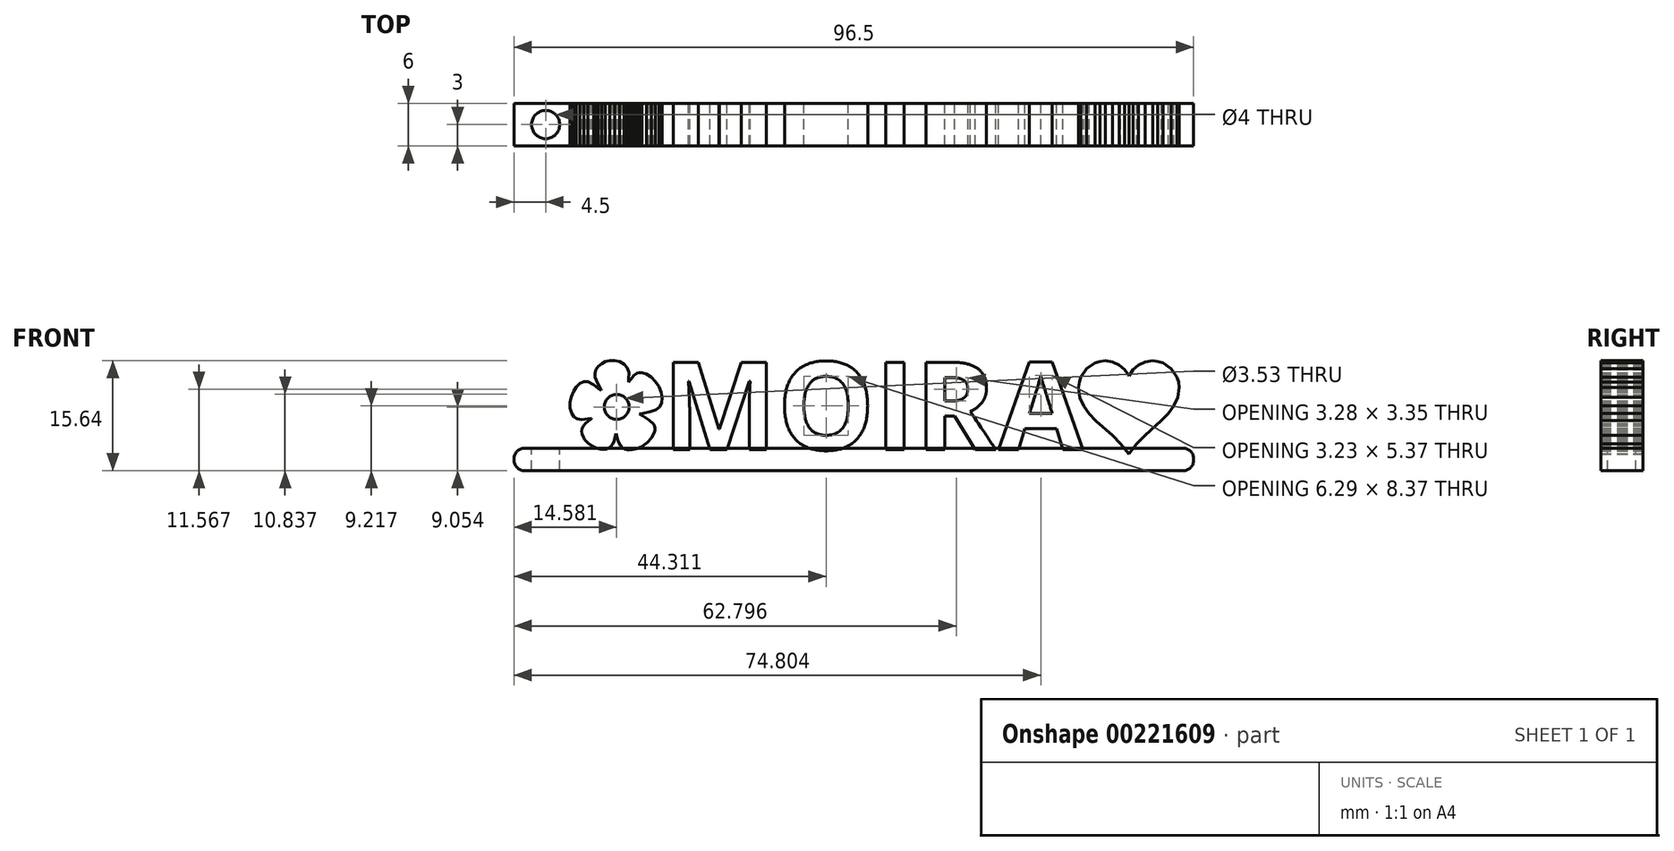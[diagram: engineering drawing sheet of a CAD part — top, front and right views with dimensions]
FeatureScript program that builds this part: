
annotation { "Feature Type Name" : "Feature", "Feature Type Description" : "" }
export const myFeature = defineFeature(function(context is Context, id is Id, definition is map)
    precondition{}
    {
        {
            var Q0;
            Q0=qCreatedBy(makeId("Front.planeOp"),FACE);
            var sketch = newSketch(context, id + "F0", { "sketchPlane" : qUnion([Q0])});
            skText(sketch, "E0", { "text": "   MOIRA", "fontName": "OpenSans-Bold.ttf"});
            skLineSegment(sketch, "E1.0.0", {"start": v(-9.3, 0.1) * mm, "end": v(-8.53, 0.46) * mm});
            skLineSegment(sketch, "E1.0.1", {"start": v(-8.53, 0.46) * mm, "end": v(-7.79, 1.02) * mm});
            skLineSegment(sketch, "E1.0.2", {"start": v(-7.79, 1.02) * mm, "end": v(-7.18, 1.67) * mm});
            skLineSegment(sketch, "E1.0.3", {"start": v(-7.18, 1.67) * mm, "end": v(-6.78, 2.35) * mm});
            skLineSegment(sketch, "E1.0.4", {"start": v(-6.78, 2.35) * mm, "end": v(-6.68, 2.7) * mm});
            skLineSegment(sketch, "E1.0.5", {"start": v(-6.68, 2.7) * mm, "end": v(-6.67, 3.02) * mm});
            skLineSegment(sketch, "E1.0.6", {"start": v(-6.67, 3.02) * mm, "end": v(-6.73, 3.33) * mm});
            skLineSegment(sketch, "E1.0.7", {"start": v(-6.73, 3.33) * mm, "end": v(-6.89, 3.62) * mm});
            skLineSegment(sketch, "E1.0.8", {"start": v(-6.89, 3.62) * mm, "end": v(-7.48, 4.2) * mm});
            skLineSegment(sketch, "E1.0.9", {"start": v(-7.48, 4.2) * mm, "end": v(-8.5, 4.79) * mm});
            skLineSegment(sketch, "E1.0.10", {"start": v(-8.5, 4.79) * mm, "end": v(-8.93, 5.06) * mm});
            skLineSegment(sketch, "E1.0.11", {"start": v(-8.93, 5.06) * mm, "end": v(-8.42, 5.16) * mm});
            skLineSegment(sketch, "E1.0.12", {"start": v(-8.42, 5.16) * mm, "end": v(-7.31, 5.37) * mm});
            skLineSegment(sketch, "E1.0.13", {"start": v(-7.31, 5.37) * mm, "end": v(-6.55, 5.65) * mm});
            skLineSegment(sketch, "E1.0.14", {"start": v(-6.55, 5.65) * mm, "end": v(-6.05, 6.04) * mm});
            skLineSegment(sketch, "E1.0.15", {"start": v(-6.05, 6.04) * mm, "end": v(-5.76, 6.58) * mm});
            skLineSegment(sketch, "E1.0.16", {"start": v(-5.76, 6.58) * mm, "end": v(-5.64, 7.33) * mm});
            skLineSegment(sketch, "E1.0.17", {"start": v(-5.64, 7.33) * mm, "end": v(-5.78, 8.14) * mm});
            skLineSegment(sketch, "E1.0.18", {"start": v(-5.78, 8.14) * mm, "end": v(-6.1, 8.93) * mm});
            skLineSegment(sketch, "E1.0.19", {"start": v(-6.1, 8.93) * mm, "end": v(-6.6, 9.67) * mm});
            skLineSegment(sketch, "E1.0.20", {"start": v(-6.6, 9.67) * mm, "end": v(-7.2, 10.28) * mm});
            skLineSegment(sketch, "E1.0.21", {"start": v(-7.2, 10.28) * mm, "end": v(-7.86, 10.72) * mm});
            skLineSegment(sketch, "E1.0.22", {"start": v(-7.86, 10.72) * mm, "end": v(-8.55, 10.93) * mm});
            skLineSegment(sketch, "E1.0.23", {"start": v(-8.55, 10.93) * mm, "end": v(-8.88, 10.93) * mm});
            skLineSegment(sketch, "E1.0.24", {"start": v(-8.88, 10.93) * mm, "end": v(-9.2, 10.85) * mm});
            skLineSegment(sketch, "E1.0.25", {"start": v(-9.2, 10.85) * mm, "end": v(-9.65, 10.56) * mm});
            skLineSegment(sketch, "E1.0.26", {"start": v(-9.65, 10.56) * mm, "end": v(-10.14, 9.98) * mm});
            skLineSegment(sketch, "E1.0.27", {"start": v(-10.14, 9.98) * mm, "end": v(-10.45, 9.58) * mm});
            skLineSegment(sketch, "E1.0.28", {"start": v(-10.45, 9.58) * mm, "end": v(-10.4, 10.03) * mm});
            skLineSegment(sketch, "E1.0.29", {"start": v(-10.4, 10.03) * mm, "end": v(-10.4, 10.93) * mm});
            skLineSegment(sketch, "E1.0.30", {"start": v(-10.4, 10.93) * mm, "end": v(-10.6, 11.63) * mm});
            skLineSegment(sketch, "E1.0.31", {"start": v(-10.6, 11.63) * mm, "end": v(-11.04, 12.15) * mm});
            skLineSegment(sketch, "E1.0.32", {"start": v(-11.04, 12.15) * mm, "end": v(-11.71, 12.5) * mm});
            skLineSegment(sketch, "E1.0.33", {"start": v(-11.71, 12.5) * mm, "end": v(-12.4, 12.64) * mm});
            skLineSegment(sketch, "E1.0.34", {"start": v(-12.4, 12.64) * mm, "end": v(-13.07, 12.62) * mm});
            skLineSegment(sketch, "E1.0.35", {"start": v(-13.07, 12.62) * mm, "end": v(-13.7, 12.47) * mm});
            skLineSegment(sketch, "E1.0.36", {"start": v(-13.7, 12.47) * mm, "end": v(-14.26, 12.2) * mm});
            skLineSegment(sketch, "E1.0.37", {"start": v(-14.26, 12.2) * mm, "end": v(-14.72, 11.83) * mm});
            skLineSegment(sketch, "E1.0.38", {"start": v(-14.72, 11.83) * mm, "end": v(-15.05, 11.38) * mm});
            skLineSegment(sketch, "E1.0.39", {"start": v(-15.05, 11.38) * mm, "end": v(-15.22, 10.87) * mm});
            skLineSegment(sketch, "E1.0.40", {"start": v(-15.22, 10.87) * mm, "end": v(-15.2, 10.3) * mm});
            skLineSegment(sketch, "E1.0.41", {"start": v(-15.2, 10.3) * mm, "end": v(-14.83, 9.4) * mm});
            skLineSegment(sketch, "E1.0.42", {"start": v(-14.83, 9.4) * mm, "end": v(-14.35, 8.55) * mm});
            skLineSegment(sketch, "E1.0.43", {"start": v(-14.35, 8.55) * mm, "end": v(-14.3, 8.4) * mm});
            skLineSegment(sketch, "E1.0.44", {"start": v(-14.3, 8.4) * mm, "end": v(-14.48, 8.53) * mm});
            skLineSegment(sketch, "E1.0.45", {"start": v(-14.48, 8.53) * mm, "end": v(-15.4, 9.23) * mm});
            skLineSegment(sketch, "E1.0.46", {"start": v(-15.4, 9.23) * mm, "end": v(-16.22, 9.63) * mm});
            skLineSegment(sketch, "E1.0.47", {"start": v(-16.22, 9.63) * mm, "end": v(-16.8, 9.63) * mm});
            skLineSegment(sketch, "E1.0.48", {"start": v(-16.8, 9.63) * mm, "end": v(-17.36, 9.37) * mm});
            skLineSegment(sketch, "E1.0.49", {"start": v(-17.36, 9.37) * mm, "end": v(-17.85, 8.9) * mm});
            skLineSegment(sketch, "E1.0.50", {"start": v(-17.85, 8.9) * mm, "end": v(-18.26, 8.26) * mm});
            skLineSegment(sketch, "E1.0.51", {"start": v(-18.26, 8.26) * mm, "end": v(-18.56, 7.51) * mm});
            skLineSegment(sketch, "E1.0.52", {"start": v(-18.56, 7.51) * mm, "end": v(-18.72, 6.71) * mm});
            skLineSegment(sketch, "E1.0.53", {"start": v(-18.72, 6.71) * mm, "end": v(-18.72, 5.9) * mm});
            skLineSegment(sketch, "E1.0.54", {"start": v(-18.72, 5.9) * mm, "end": v(-18.52, 5.16) * mm});
            skLineSegment(sketch, "E1.0.55", {"start": v(-18.52, 5.16) * mm, "end": v(-18.2, 4.64) * mm});
            skLineSegment(sketch, "E1.0.56", {"start": v(-18.2, 4.64) * mm, "end": v(-17.75, 4.36) * mm});
            skLineSegment(sketch, "E1.0.57", {"start": v(-17.75, 4.36) * mm, "end": v(-17.1, 4.27) * mm});
            skLineSegment(sketch, "E1.0.58", {"start": v(-17.1, 4.27) * mm, "end": v(-16.21, 4.37) * mm});
            skLineSegment(sketch, "E1.0.59", {"start": v(-16.21, 4.37) * mm, "end": v(-15.7, 4.43) * mm});
            skLineSegment(sketch, "E1.0.60", {"start": v(-15.7, 4.43) * mm, "end": v(-15.67, 4.4) * mm});
            skLineSegment(sketch, "E1.0.61", {"start": v(-15.67, 4.4) * mm, "end": v(-15.78, 4.33) * mm});
            skLineSegment(sketch, "E1.0.62", {"start": v(-15.78, 4.33) * mm, "end": v(-16.17, 4.07) * mm});
            skLineSegment(sketch, "E1.0.63", {"start": v(-16.17, 4.07) * mm, "end": v(-16.55, 3.71) * mm});
            skLineSegment(sketch, "E1.0.64", {"start": v(-16.55, 3.71) * mm, "end": v(-16.87, 3.33) * mm});
            skLineSegment(sketch, "E1.0.65", {"start": v(-16.87, 3.33) * mm, "end": v(-17.04, 3) * mm});
            skLineSegment(sketch, "E1.0.66", {"start": v(-17.04, 3) * mm, "end": v(-17.08, 2.6) * mm});
            skLineSegment(sketch, "E1.0.67", {"start": v(-17.08, 2.6) * mm, "end": v(-17.02, 2.2) * mm});
            skLineSegment(sketch, "E1.0.68", {"start": v(-17.02, 2.2) * mm, "end": v(-16.87, 1.78) * mm});
            skLineSegment(sketch, "E1.0.69", {"start": v(-16.87, 1.78) * mm, "end": v(-16.62, 1.39) * mm});
            skLineSegment(sketch, "E1.0.70", {"start": v(-16.62, 1.39) * mm, "end": v(-16.3, 1.02) * mm});
            skLineSegment(sketch, "E1.0.71", {"start": v(-16.3, 1.02) * mm, "end": v(-15.9, 0.69) * mm});
            skLineSegment(sketch, "E1.0.72", {"start": v(-15.9, 0.69) * mm, "end": v(-15.45, 0.4) * mm});
            skLineSegment(sketch, "E1.0.73", {"start": v(-15.45, 0.4) * mm, "end": v(-14.95, 0.2) * mm});
            skLineSegment(sketch, "E1.0.74", {"start": v(-14.95, 0.2) * mm, "end": v(-14.44, 0.06) * mm});
            skLineSegment(sketch, "E1.0.75", {"start": v(-14.44, 0.06) * mm, "end": v(-13.98, 0.02) * mm});
            skLineSegment(sketch, "E1.0.76", {"start": v(-13.98, 0.02) * mm, "end": v(-13.58, 0.08) * mm});
            skLineSegment(sketch, "E1.0.77", {"start": v(-13.58, 0.08) * mm, "end": v(-13.23, 0.23) * mm});
            skLineSegment(sketch, "E1.0.78", {"start": v(-13.23, 0.23) * mm, "end": v(-12.92, 0.49) * mm});
            skLineSegment(sketch, "E1.0.79", {"start": v(-12.92, 0.49) * mm, "end": v(-12.67, 0.84) * mm});
            skLineSegment(sketch, "E1.0.80", {"start": v(-12.67, 0.84) * mm, "end": v(-12.46, 1.28) * mm});
            skLineSegment(sketch, "E1.0.81", {"start": v(-12.46, 1.28) * mm, "end": v(-12.3, 1.83) * mm});
            skLineSegment(sketch, "E1.0.82", {"start": v(-12.3, 1.83) * mm, "end": v(-12.19, 2.26) * mm});
            skLineSegment(sketch, "E1.0.83", {"start": v(-12.19, 2.26) * mm, "end": v(-12.13, 2.1) * mm});
            skLineSegment(sketch, "E1.0.84", {"start": v(-12.13, 2.1) * mm, "end": v(-12.01, 1.53) * mm});
            skLineSegment(sketch, "E1.0.85", {"start": v(-12.01, 1.53) * mm, "end": v(-11.82, 1) * mm});
            skLineSegment(sketch, "E1.0.86", {"start": v(-11.82, 1) * mm, "end": v(-11.6, 0.55) * mm});
            skLineSegment(sketch, "E1.0.87", {"start": v(-11.6, 0.55) * mm, "end": v(-11.35, 0.26) * mm});
            skLineSegment(sketch, "E1.0.88", {"start": v(-11.35, 0.26) * mm, "end": v(-10.95, 0.05) * mm});
            skLineSegment(sketch, "E1.0.89", {"start": v(-10.95, 0.05) * mm, "end": v(-10.46, -0.04) * mm});
            skLineSegment(sketch, "E1.0.90", {"start": v(-10.46, -0.04) * mm, "end": v(-9.9, -0.03) * mm});
            skLineSegment(sketch, "E1.0.91", {"start": v(-9.9, -0.03) * mm, "end": v(-9.3, 0.1) * mm});
            skCircle(sketch, "E2", {"center": v(-12.12, 6.05) * mm, "radius": 1.77 * mm});
            skLineSegment(sketch, "E3", {"start": v(57.24, 12.6) * mm, "end": v(56.48, 12.52) * mm});
            skLineSegment(sketch, "E4", {"start": v(56.48, 12.52) * mm, "end": v(55.78, 12.3) * mm});
            skLineSegment(sketch, "E5", {"start": v(55.78, 12.3) * mm, "end": v(54.58, 11.5) * mm});
            skLineSegment(sketch, "E6", {"start": v(54.58, 11.5) * mm, "end": v(53.77, 10.3) * mm});
            skLineSegment(sketch, "E7", {"start": v(53.77, 10.3) * mm, "end": v(53.55, 9.59) * mm});
            skLineSegment(sketch, "E8", {"start": v(53.55, 9.59) * mm, "end": v(53.48, 8.83) * mm});
            skLineSegment(sketch, "E9", {"start": v(53.48, 8.83) * mm, "end": v(53.66, 7.39) * mm});
            skLineSegment(sketch, "E10", {"start": v(53.66, 7.39) * mm, "end": v(54.19, 6.16) * mm});
            skLineSegment(sketch, "E11", {"start": v(54.19, 6.16) * mm, "end": v(54.97, 5.08) * mm});
            skLineSegment(sketch, "E12", {"start": v(54.97, 5.08) * mm, "end": v(55.95, 4.08) * mm});
            skLineSegment(sketch, "E13", {"start": v(55.95, 4.08) * mm, "end": v(58.25, 2.03) * mm});
            skLineSegment(sketch, "E14", {"start": v(58.25, 2.03) * mm, "end": v(59.44, 0.82) * mm});
            skLineSegment(sketch, "E15", {"start": v(59.44, 0.82) * mm, "end": v(60.56, -0.59) * mm});
            skLineSegment(sketch, "E16", {"start": v(60.56, -0.59) * mm, "end": v(60.6, -0.65) * mm});
            skLineSegment(sketch, "E17", {"start": v(60.6, -0.65) * mm, "end": v(60.65, -0.59) * mm});
            skLineSegment(sketch, "E18", {"start": v(60.65, -0.59) * mm, "end": v(61.72, 0.82) * mm});
            skLineSegment(sketch, "E19", {"start": v(61.72, 0.82) * mm, "end": v(62.89, 2.03) * mm});
            skLineSegment(sketch, "E20", {"start": v(62.89, 2.03) * mm, "end": v(65.2, 4.12) * mm});
            skLineSegment(sketch, "E21", {"start": v(65.2, 4.12) * mm, "end": v(66.2, 5.13) * mm});
            skLineSegment(sketch, "E22", {"start": v(66.2, 5.13) * mm, "end": v(67, 6.21) * mm});
            skLineSegment(sketch, "E23", {"start": v(67, 6.21) * mm, "end": v(67.53, 7.42) * mm});
            skLineSegment(sketch, "E24", {"start": v(67.53, 7.42) * mm, "end": v(67.73, 8.83) * mm});
            skLineSegment(sketch, "E25", {"start": v(67.73, 8.83) * mm, "end": v(67.65, 9.59) * mm});
            skLineSegment(sketch, "E26", {"start": v(67.65, 9.59) * mm, "end": v(67.43, 10.3) * mm});
            skLineSegment(sketch, "E27", {"start": v(67.43, 10.3) * mm, "end": v(66.62, 11.5) * mm});
            skLineSegment(sketch, "E28", {"start": v(66.62, 11.5) * mm, "end": v(65.43, 12.3) * mm});
            skLineSegment(sketch, "E29", {"start": v(65.43, 12.3) * mm, "end": v(64.72, 12.52) * mm});
            skLineSegment(sketch, "E30", {"start": v(64.72, 12.52) * mm, "end": v(63.96, 12.6) * mm});
            skLineSegment(sketch, "E31", {"start": v(63.96, 12.6) * mm, "end": v(62.9, 12.44) * mm});
            skLineSegment(sketch, "E32", {"start": v(62.9, 12.44) * mm, "end": v(61.96, 12.01) * mm});
            skLineSegment(sketch, "E33", {"start": v(61.96, 12.01) * mm, "end": v(61.18, 11.35) * mm});
            skLineSegment(sketch, "E34", {"start": v(61.18, 11.35) * mm, "end": v(60.6, 10.5) * mm});
            skLineSegment(sketch, "E35", {"start": v(60.6, 10.5) * mm, "end": v(60.02, 11.35) * mm});
            skLineSegment(sketch, "E36", {"start": v(60.02, 11.35) * mm, "end": v(59.24, 12.01) * mm});
            skLineSegment(sketch, "E37", {"start": v(59.24, 12.01) * mm, "end": v(58.3, 12.44) * mm});
            skLineSegment(sketch, "E38", {"start": v(58.3, 12.44) * mm, "end": v(57.24, 12.6) * mm});
            skLineSegment(sketch, "E39", {"start": v(54.8, 12.5) * mm, "end": v(72.66, 12.5) * mm, "construction": true});
            const initialGuessF0  = {"E0": [-0.0192, 0, 1, 0, 0.0125]};
            skSetInitialGuess(sketch, initialGuessF0);
            skSolve(sketch);
        }
        {
            var Q0;
            Q0=qSketchRegion(id+"F0",true);
            extrude(context, id + "F1", {"entities" : qUnion([Q0]), "endBound" : BoundingType.SYMMETRIC, "depth" : 6 * mm});
        }
        {
            var Q0;
            Q0=qCreatedBy(makeId("Top.planeOp"),FACE);
            var sketch = newSketch(context, id + "F2", { "sketchPlane" : qUnion([Q0])});
            skLineSegment(sketch, "E40.bottom", {"start": v(-19.2, 3) * mm, "end": v(69.8, 3) * mm});
            skLineSegment(sketch, "E40.top", {"start": v(-19.2, -3) * mm, "end": v(69.8, -3) * mm});
            skLineSegment(sketch, "E40.left", {"start": v(-19.2, 3) * mm, "end": v(-19.2, -3) * mm});
            skLineSegment(sketch, "E40.right", {"start": v(69.8, 3) * mm, "end": v(69.8, -3) * mm});
            skSolve(sketch);
        }
        {
            var Q0;
            Q0=makeQuery(id+"F2.imprint","IMPRINT",FACE,{"disambiguationData":[TD([[makeQuery(id+"F2.imprint","IMPRINT",EDGE,{"derivedFrom":sQuery(id+"F2.wireOp",EDGE,"E40.bottom")}),-1.0]])]});
            extrude(context, id + "F3", {"entities" : qUnion([Q0]), "depth" : 0.2 * mm});
        }
        {
            var Q0;
            Q0=makeQuery(id+"F3.opExtrude","CAP_FACE",FACE,{"disambiguationData":[OSD([sQuery(id+"F2.wireOp",EDGE,"E40.bottom"),sQuery(id+"F2.wireOp",EDGE,"E40.top"),sQuery(id+"F2.wireOp",EDGE,"E40.left"),sQuery(id+"F2.wireOp",EDGE,"E40.right")])],"isStart":true});
            extrude(context, id + "F4", {"entities" : qUnion([Q0]), "depth" : 3 * mm});
        }
        {
            var Q0;
            {var subQ0=sQuery(id+"F2.wireOp",EDGE,"E40.left");Q0=makeQuery(id+"FaVoHrOpcFZXiYX_6.opBoolean","MERGE",FACE,{"derivedFrom":[makeQuery(id+"F3.opExtrude","SWEPT_FACE",FACE,{"disambiguationData":[OSD([subQ0])]}),makeQuery(id+"F4.opExtrude","SWEPT_FACE",FACE,{"disambiguationData":[OSD([subQ0])]})]});}
            var sketch = newSketch(context, id + "F5", { "sketchPlane" : qUnion([Q0])});
            skLineSegment(sketch, "E41.bottom", {"start": v(-3, -3) * mm, "end": v(3, -3) * mm});
            skLineSegment(sketch, "E41.top", {"start": v(-3, 0.2) * mm, "end": v(3, 0.2) * mm});
            skLineSegment(sketch, "E41.left", {"start": v(-3, -3) * mm, "end": v(-3, 0.2) * mm});
            skLineSegment(sketch, "E41.right", {"start": v(3, -3) * mm, "end": v(3, 0.2) * mm});
            skSolve(sketch);
        }
        {
            var Q0;
            Q0=qSketchRegion(id+"F5",true);
            extrude(context, id + "F6", {"entities" : qUnion([Q0]), "operationType" : NewBodyOperationType.ADD, "depth" : 7.5 * mm});
        }
        {
            var Q0;
            Q0=makeQuery(id+"F6.opExtrude","CAP_EDGE",EDGE,{"disambiguationData":[OSD([sQuery(id+"F5.wireOp",EDGE,"E41.bottom")])],"isStart":false});
            var Q1;
            Q1=makeQuery(id+"F6.opExtrude","CAP_EDGE",EDGE,{"disambiguationData":[OSD([sQuery(id+"F5.wireOp",EDGE,"E41.top")])],"isStart":false});
            var Q2;
            Q2=makeQuery(id+"F4.opExtrude","CAP_EDGE",EDGE,{"disambiguationData":[OSD([sQuery(id+"F2.wireOp",EDGE,"E40.right")])],"isStart":false});
            fillet(context, id + "F7", {"entities" : qUnion([Q0, Q1, Q2]), "radius" : 1.5 * mm, "tangentPropagation" : true, "allowEdgeOverflow" : false});
        }
        {
            var Q0;
            {var subQ19=sQuery(id+"F2.wireOp",EDGE,"E40.top");var subQ20=sQuery(id+"F2.wireOp",EDGE,"E40.bottom");var subQ63=sQuery(id+"F0.wireOp",EDGE,"E0.sketch_text.stroke-2");var subQ66=sQuery(id+"F2.wireOp",EDGE,"E40.left");Q0=makeQuery(id+"F6.boolean.opBoolean","MERGE",FACE,{"derivedFrom":[makeQuery(id+"FaVoHrOpcFZXiYX_6.opBoolean","SPLIT",FACE,{"disambiguationData":[TD([makeQuery(id+"F1.opExtrude","SWEPT_FACE",FACE,{"disambiguationData":[OSD([subQ63])]})])],"derivedFrom":makeQuery(id+"F3.opExtrude","CAP_FACE",FACE,{"disambiguationData":[OSD([subQ20,subQ19,subQ66,sQuery(id+"F2.wireOp",EDGE,"E40.right")])],"isStart":false})}),makeQuery(id+"F6.opExtrude","SWEPT_FACE",FACE,{"disambiguationData":[OSD([sQuery(id+"F5.wireOp",EDGE,"E41.top")])]})]});}
            var sketch = newSketch(context, id + "F8", { "sketchPlane" : qUnion([Q0])});
            skCircle(sketch, "E42", {"center": v(-22.2, 0) * mm, "radius": 2 * mm});
            skSolve(sketch);
        }
        {
            var Q0;
            Q0=makeQuery(id+"F8.imprint","IMPRINT",FACE,{"disambiguationData":[TD([[makeQuery(id+"F8.imprint","IMPRINT",EDGE,{"derivedFrom":sQuery(id+"F8.wireOp",EDGE,"E42")}),1.0]])]});
            extrude(context, id + "F9", {"entities" : qUnion([Q0]), "operationType" : NewBodyOperationType.REMOVE, "oppositeDirection" : true, "depth" : 4 * mm});
        }
        {
            var Q0;
            Q0=makeQuery(id+"F3.opExtrude","CAP_EDGE",EDGE,{"disambiguationData":[OSD([sQuery(id+"F2.wireOp",EDGE,"E40.right")])],"isStart":false});
            fillet(context, id + "F10", {"entities" : qUnion([Q0]), "radius" : 1.5 * mm, "tangentPropagation" : true, "allowEdgeOverflow" : false});
        }
    });
